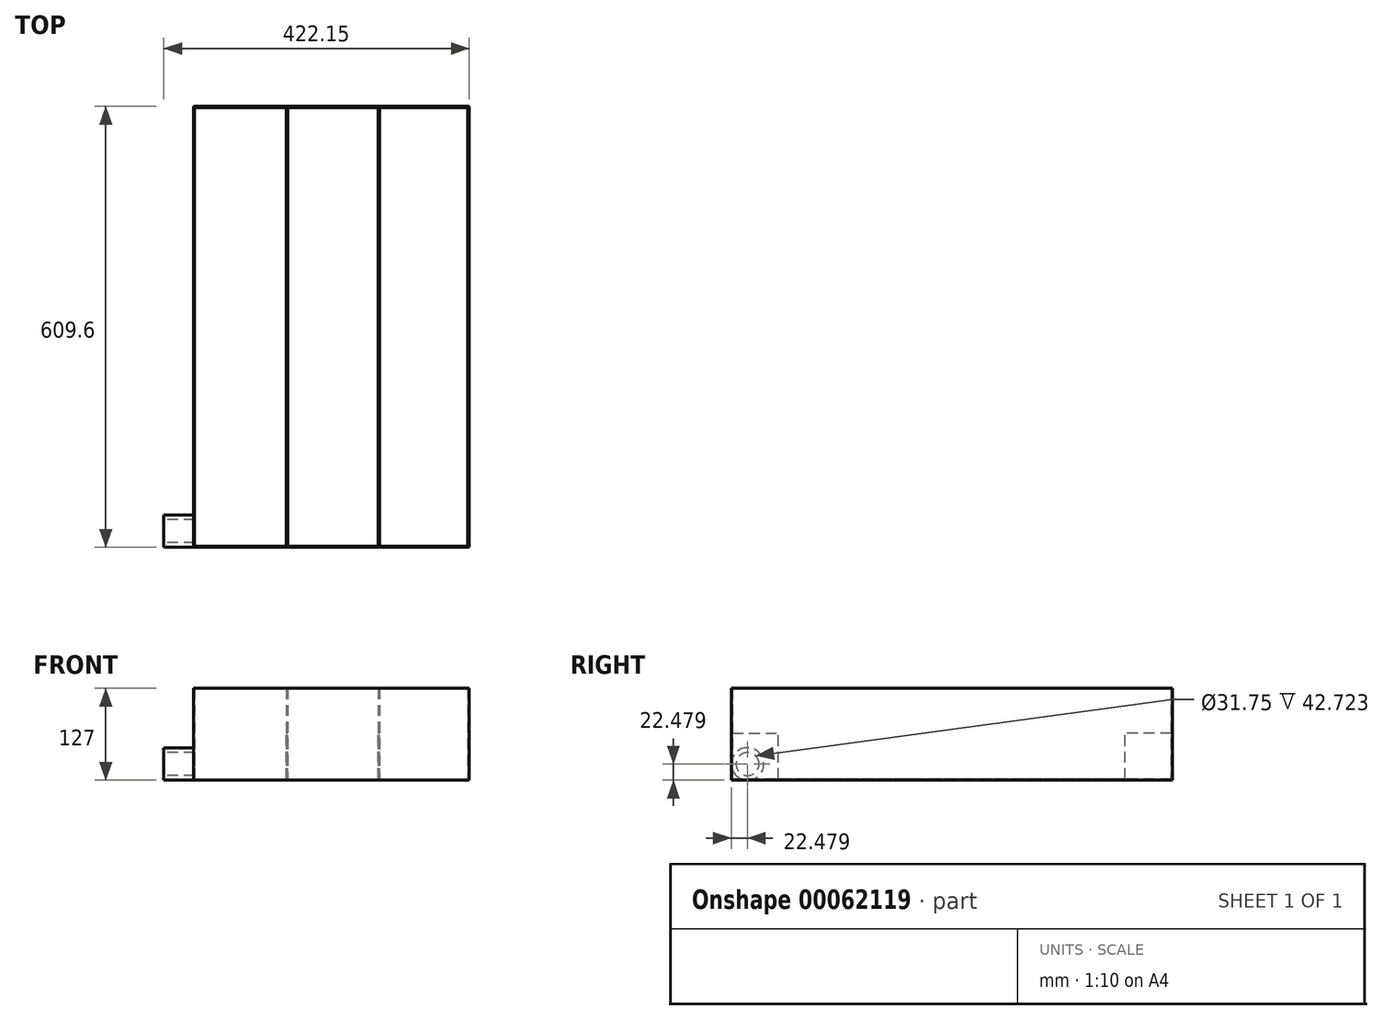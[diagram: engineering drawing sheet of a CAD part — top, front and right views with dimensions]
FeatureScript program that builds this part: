
annotation { "Feature Type Name" : "Feature", "Feature Type Description" : "" }
export const myFeature = defineFeature(function(context is Context, id is Id, definition is map)
    precondition{}
    {
        {
            var Q0;
            Q0=qCreatedBy(makeId("Top.planeOp"),FACE);
            var sketch = newSketch(context, id + "F0", { "sketchPlane" : qUnion([Q0])});
            skLineSegment(sketch, "E0.bottom", {"start": v(0, 0) * mm, "end": v(381, 0) * mm});
            skLineSegment(sketch, "E0.top", {"start": v(0, 609.6) * mm, "end": v(381, 609.6) * mm});
            skLineSegment(sketch, "E0.left", {"start": v(0, 0) * mm, "end": v(0, 609.6) * mm});
            skLineSegment(sketch, "E0.right", {"start": v(381, 0) * mm, "end": v(381, 609.6) * mm});
            skSolve(sketch);
        }
        {
            var Q0;
            Q0=makeQuery(id+"F0.imprint","IMPRINT",FACE,{"disambiguationData":[TD([[makeQuery(id+"F0.imprint","IMPRINT",EDGE,{"derivedFrom":sQuery(id+"F0.wireOp",EDGE,"E0.bottom")}),1.0]])]});
            extrude(context, id + "F1", {"entities" : qUnion([Q0]), "depth" : 127 * mm});
        }
        {
            var Q0;
            Q0=makeQuery(id+"F1.opExtrude","CAP_FACE",FACE,{"disambiguationData":[OSD([sQuery(id+"F0.wireOp",EDGE,"E0.bottom"),sQuery(id+"F0.wireOp",EDGE,"E0.top"),sQuery(id+"F0.wireOp",EDGE,"E0.left"),sQuery(id+"F0.wireOp",EDGE,"E0.right")])],"isStart":false});
            shell(context, id + "F2", {"entities" : qUnion([Q0]), "thickness" : 1.57 * mm});
        }
        {
            var Q0;
            Q0=makeQuery(id+"F2.opShell","OFFSET_FACE",FACE,{"disambiguationData":[OSD([sQuery(id+"F0.wireOp",EDGE,"E0.bottom"),sQuery(id+"F0.wireOp",EDGE,"E0.top"),sQuery(id+"F0.wireOp",EDGE,"E0.left"),sQuery(id+"F0.wireOp",EDGE,"E0.right")])]});
            var sketch = newSketch(context, id + "F3", { "sketchPlane" : qUnion([Q0])});
            skLineSegment(sketch, "E1", {"start": v(128.57, 608.03) * mm, "end": v(128.57, 1.57) * mm});
            skLineSegment(sketch, "E2", {"start": v(255.57, 608.03) * mm, "end": v(255.57, 1.57) * mm});
            skLineSegment(sketch, "E3.0", {"start": v(130.15, 608.03) * mm, "end": v(130.15, 1.57) * mm});
            skLineSegment(sketch, "E4.0", {"start": v(257.15, 608.03) * mm, "end": v(257.15, 1.57) * mm});
            skSolve(sketch);
        }
        {
            var Q0;
            {var subQ0=sQuery(id+"F3.wireOp",EDGE,"E1");Q0=makeQuery(id+"F3.imprint","IMPRINT",FACE,{"disambiguationData":[TD([[makeQuery(id+"F3.imprint","IMPRINT",EDGE,{"derivedFrom":subQ0}),1.0]])]});}
            var Q1;
            {var subQ0=sQuery(id+"F3.wireOp",EDGE,"E2");Q1=makeQuery(id+"F3.imprint","IMPRINT",FACE,{"disambiguationData":[TD([[makeQuery(id+"F3.imprint","IMPRINT",EDGE,{"derivedFrom":subQ0}),1.0]])]});}
            var Q2;
            Q2=makeQuery(id+"F1.opExtrude","CAP_FACE",FACE,{"disambiguationData":[OSD([sQuery(id+"F0.wireOp",EDGE,"E0.bottom"),sQuery(id+"F0.wireOp",EDGE,"E0.top"),sQuery(id+"F0.wireOp",EDGE,"E0.left"),sQuery(id+"F0.wireOp",EDGE,"E0.right")])],"isStart":false});
            extrude(context, id + "F4", {"entities" : qUnion([Q0, Q1]), "operationType" : NewBodyOperationType.ADD, "endBound" : BoundingType.UP_TO_SURFACE, "endBoundEntityFace" : qUnion([Q2]), "depth" : 25.4 * mm});
        }
        {
            var Q0;
            Q0=makeQuery(id+"F4.opExtrude","SWEPT_FACE",FACE,{"disambiguationData":[OSD([sQuery(id+"F3.wireOp",EDGE,"E4.0")])]});
            var sketch = newSketch(context, id + "F5", { "sketchPlane" : qUnion([Q0])});
            skLineSegment(sketch, "E5.bottom", {"start": v(1.57, 1.57) * mm, "end": v(65.07, 1.57) * mm});
            skLineSegment(sketch, "E5.top", {"start": v(1.57, 65.07) * mm, "end": v(65.07, 65.07) * mm});
            skLineSegment(sketch, "E5.left", {"start": v(1.57, 1.57) * mm, "end": v(1.57, 65.07) * mm});
            skLineSegment(sketch, "E5.right", {"start": v(65.07, 1.57) * mm, "end": v(65.07, 65.07) * mm});
            skSolve(sketch);
        }
        {
            var Q0;
            Q0=makeQuery(id+"F5.imprint","IMPRINT",FACE,{"disambiguationData":[TD([[makeQuery(id+"F5.imprint","IMPRINT",EDGE,{"derivedFrom":sQuery(id+"F5.wireOp",EDGE,"E5.bottom")}),-1.0]])]});
            var Q1;
            Q1=makeQuery(id+"F4.opExtrude","SWEPT_FACE",FACE,{"disambiguationData":[OSD([sQuery(id+"F3.wireOp",EDGE,"E3.0")])]});
            extrude(context, id + "F6", {"entities" : qUnion([Q0]), "operationType" : NewBodyOperationType.REMOVE, "endBound" : BoundingType.UP_TO_SURFACE, "oppositeDirection" : true, "endBoundEntityFace" : qUnion([Q1]), "depth" : 25.4 * mm});
        }
        {
            var Q0;
            Q0=makeQuery(id+"F4.opExtrude","SWEPT_FACE",FACE,{"disambiguationData":[OSD([sQuery(id+"F3.wireOp",EDGE,"E3.0")])]});
            var sketch = newSketch(context, id + "F7", { "sketchPlane" : qUnion([Q0])});
            skLineSegment(sketch, "E6.bottom", {"start": v(608.03, 1.57) * mm, "end": v(544.53, 1.57) * mm});
            skLineSegment(sketch, "E6.top", {"start": v(608.03, 65.07) * mm, "end": v(544.53, 65.07) * mm});
            skLineSegment(sketch, "E6.left", {"start": v(608.03, 1.57) * mm, "end": v(608.03, 65.07) * mm});
            skLineSegment(sketch, "E6.right", {"start": v(544.53, 1.57) * mm, "end": v(544.53, 65.07) * mm});
            skSolve(sketch);
        }
        {
            var Q0;
            Q0=makeQuery(id+"F7.imprint","IMPRINT",FACE,{"disambiguationData":[TD([[makeQuery(id+"F7.imprint","IMPRINT",EDGE,{"derivedFrom":sQuery(id+"F7.wireOp",EDGE,"E6.bottom")}),-1.0]])]});
            var Q1;
            Q1=makeQuery(id+"F2.opShell","OFFSET_FACE",FACE,{"disambiguationData":[OSD([sQuery(id+"F0.wireOp",EDGE,"E0.left")])]});
            extrude(context, id + "F8", {"entities" : qUnion([Q0]), "operationType" : NewBodyOperationType.REMOVE, "endBound" : BoundingType.UP_TO_SURFACE, "oppositeDirection" : true, "endBoundEntityFace" : qUnion([Q1]), "depth" : 25.4 * mm});
        }
        {
            var Q0;
            Q0=makeQuery(id+"F1.opExtrude","SWEPT_FACE",FACE,{"disambiguationData":[OSD([sQuery(id+"F0.wireOp",EDGE,"E0.left")])]});
            var sketch = newSketch(context, id + "F9", { "sketchPlane" : qUnion([Q0])});
            skCircle(sketch, "E7", {"center": v(-22.48, 22.48) * mm, "radius": 22.48 * mm});
            skSolve(sketch);
        }
        {
            var Q0;
            Q0 = qSketchRegion(id + "F9", true);
            extrude(context, id + "F10", {"entities" : qUnion([Q0]), "operationType" : NewBodyOperationType.ADD, "depth" : 41.15 * mm});
        }
        {
            var Q0;
            Q0=makeQuery(id+"F10.opExtrude","CAP_FACE",FACE,{"disambiguationData":[OSD([sQuery(id+"F9.wireOp",EDGE,"E7")])],"isStart":false});
            var sketch = newSketch(context, id + "F11", { "sketchPlane" : qUnion([Q0])});
            skCircle(sketch, "E8", {"center": v(-22.48, 22.48) * mm, "radius": 15.88 * mm});
            skSolve(sketch);
        }
        {
            var Q0;
            Q0 = qSketchRegion(id + "F11", true);
            var Q1;
            Q1=makeQuery(id+"F2.opShell","OFFSET_FACE",FACE,{"disambiguationData":[OSD([sQuery(id+"F0.wireOp",EDGE,"E0.left")])]});
            extrude(context, id + "F12", {"entities" : qUnion([Q0]), "operationType" : NewBodyOperationType.REMOVE, "endBound" : BoundingType.UP_TO_SURFACE, "oppositeDirection" : true, "endBoundEntityFace" : qUnion([Q1]), "depth" : 25.4 * mm});
        }
    });
